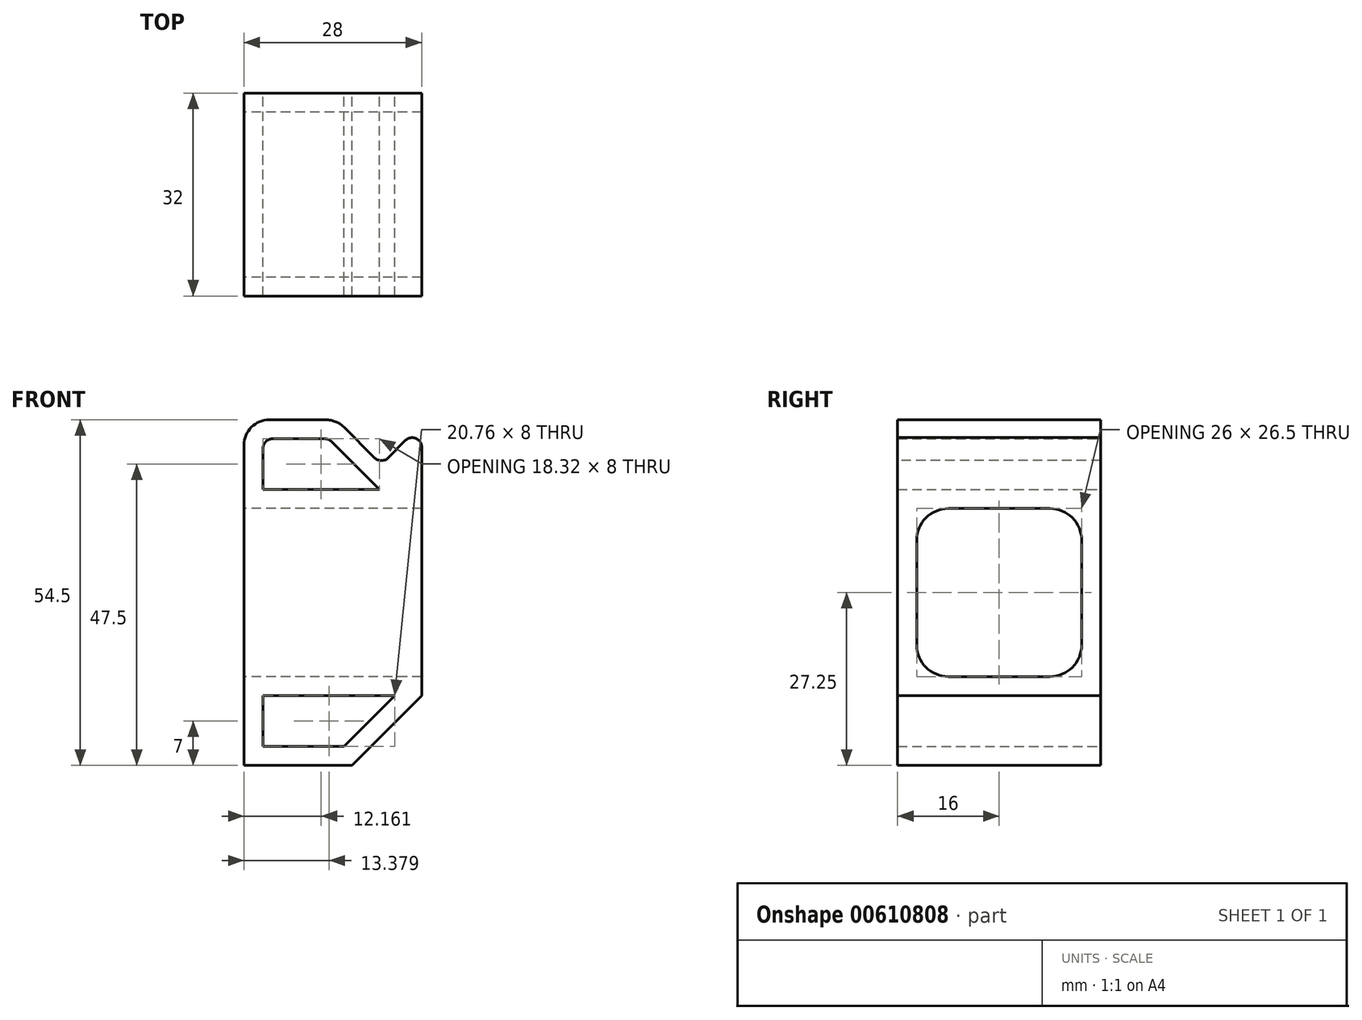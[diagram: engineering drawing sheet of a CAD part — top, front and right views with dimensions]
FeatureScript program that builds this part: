
annotation { "Feature Type Name" : "Feature", "Feature Type Description" : "" }
export const myFeature = defineFeature(function(context is Context, id is Id, definition is map)
    precondition{}
    {
        {
            var Q0;
            Q0=qCreatedBy(makeId("Right.planeOp"),FACE);
            var sketch = newSketch(context, id + "F0", { "sketchPlane" : qUnion([Q0])});
            skLineSegment(sketch, "E0.bottom", {"start": v(13, 13.25) * mm, "end": v(-13, 13.25) * mm});
            skLineSegment(sketch, "E0.top", {"start": v(13, -13.25) * mm, "end": v(-13, -13.25) * mm});
            skLineSegment(sketch, "E0.left", {"start": v(13, 13.25) * mm, "end": v(13, -13.25) * mm});
            skLineSegment(sketch, "E0.right", {"start": v(-13, 13.25) * mm, "end": v(-13, -13.25) * mm});
            skPoint(sketch, "E0.middle", {"position": v(0, 0) * mm});
            skLineSegment(sketch, "E1.bottom", {"start": v(16, 16.25) * mm, "end": v(-16, 16.25) * mm});
            skLineSegment(sketch, "E1.top", {"start": v(16, -16.25) * mm, "end": v(-16, -16.25) * mm});
            skLineSegment(sketch, "E1.left", {"start": v(16, 16.25) * mm, "end": v(16, -16.25) * mm});
            skLineSegment(sketch, "E1.right", {"start": v(-16, 16.25) * mm, "end": v(-16, -16.25) * mm});
            skSolve(sketch);
        }
        {
            var Q0;
            Q0 = qSketchRegion(id + "F0", true);
            extrude(context, id + "F1", {"entities" : qUnion([Q0]), "depth" : 28 * mm, "offsetDistance" : 25 * mm});
        }
        {
            var Q0;
            Q0=qCreatedBy(makeId("Front.planeOp"),FACE);
            var sketch = newSketch(context, id + "F2", { "sketchPlane" : qUnion([Q0])});
            skLineSegment(sketch, "E2", {"start": v(28, 16.25) * mm, "end": v(28, 26.54) * mm});
            skLineSegment(sketch, "E3", {"start": v(28, 26.54) * mm, "end": v(21.64, 20.18) * mm});
            skLineSegment(sketch, "E4", {"start": v(21.64, 20.18) * mm, "end": v(14.56, 27.25) * mm});
            skLineSegment(sketch, "E5", {"start": v(14.56, 27.25) * mm, "end": v(0, 27.25) * mm});
            skLineSegment(sketch, "E6", {"start": v(0, 27.25) * mm, "end": v(0, 16.25) * mm});
            skLineSegment(sketch, "E7.0", {"start": v(21.32, 16.25) * mm, "end": v(3, 16.25) * mm});
            skLineSegment(sketch, "E7.1", {"start": v(3, 24.25) * mm, "end": v(3, 16.25) * mm});
            skLineSegment(sketch, "E7.2", {"start": v(13.32, 24.25) * mm, "end": v(3, 24.25) * mm});
            skLineSegment(sketch, "E7.3", {"start": v(21.32, 16.25) * mm, "end": v(13.32, 24.25) * mm});
            skLineSegment(sketch, "E8", {"start": v(0, 16.25) * mm, "end": v(28, 16.25) * mm});
            skLineSegment(sketch, "E9.2", {"start": v(45.18, 16.25) * mm, "end": v(-18.36, 16.25) * mm, "construction": true});
            skSolve(sketch);
        }
        {
            var Q0;
            {var subQ0=sQuery(id+"F2.wireOp",EDGE,"E2");Q0=makeQuery(id+"F2.imprint","IMPRINT",FACE,{"disambiguationData":[TD([[makeQuery(id+"F2.imprint","IMPRINT",EDGE,{"derivedFrom":subQ0}),1.0]])]});}
            var Q1;
            Q1=makeQuery(id+"F1.opExtrude","SWEPT_FACE",FACE,{"disambiguationData":[OSD([sQuery(id+"F0.wireOp",EDGE,"E1.right")])]});
            var Q2;
            Q2=makeQuery(id+"F1.opExtrude","SWEPT_FACE",FACE,{"disambiguationData":[OSD([sQuery(id+"F0.wireOp",EDGE,"ShcMqtXd-iH10-RJuc-bSqI-YvODFhP9SOUm")])]});
            extrude(context, id + "F3", {"entities" : qUnion([Q0]), "operationType" : NewBodyOperationType.ADD, "endBound" : BoundingType.SYMMETRIC, "depth" : 32 * mm, "endBoundEntityFace" : qUnion([Q1]), "offsetDistance" : 25 * mm, "hasSecondDirection" : true, "secondDirectionBound" : SecondDirectionBoundingType.UP_TO_SURFACE, "secondDirectionOppositeDirection" : true, "secondDirectionDepth" : 25 * mm, "secondDirectionBoundEntityFace" : qUnion([Q2])});
        }
        {
            var Q0;
            Q0=qCreatedBy(makeId("Front.planeOp"),FACE);
            var sketch = newSketch(context, id + "F4", { "sketchPlane" : qUnion([Q0])});
            skLineSegment(sketch, "E10.0.1", {"start": v(0, -16.25) * mm, "end": v(28, -16.25) * mm});
            skLineSegment(sketch, "E11.bottom", {"start": v(0, -27.25) * mm, "end": v(17, -27.25) * mm});
            skLineSegment(sketch, "E11.right", {"start": v(0, -16.25) * mm, "end": v(0, -27.25) * mm});
            skLineSegment(sketch, "E12", {"start": v(28, -16.25) * mm, "end": v(17, -27.25) * mm});
            skLineSegment(sketch, "E13.0", {"start": v(23.76, -16.25) * mm, "end": v(15.76, -24.25) * mm});
            skLineSegment(sketch, "E13.1", {"start": v(3, -24.25) * mm, "end": v(15.76, -24.25) * mm});
            skLineSegment(sketch, "E13.2", {"start": v(3, -16.25) * mm, "end": v(3, -24.25) * mm});
            skSolve(sketch);
        }
        {
            var Q0;
            Q0=makeQuery(id+"F4.imprint","IMPRINT",FACE,{"disambiguationData":[TD([[makeQuery(id+"F4.imprint","IMPRINT",EDGE,{"derivedFrom":sQuery(id+"F4.wireOp",EDGE,"E11.bottom")}),1.0]])]});
            var Q1;
            Q1=makeQuery(id+"F1.opExtrude","CAP_VERTEX",VERTEX,{"disambiguationData":[OSD([sQuery(id+"F0.wireOp",EDGE,"E1.top"),sQuery(id+"F0.wireOp",EDGE,"E1.right"),sQuery(id+"F0.wireOp",EDGE,"f836a4ea-6556-4c57-9a7b-fc94dc2d46c80.MirrorCS")])],"isStart":false});
            var Q2;
            Q2=makeQuery(id+"F1.opExtrude","CAP_VERTEX",VERTEX,{"disambiguationData":[OSD([sQuery(id+"F0.wireOp",EDGE,"E1.top"),sQuery(id+"F0.wireOp",EDGE,"E1.left"),sQuery(id+"F0.wireOp",EDGE,"1c46fe3f-ea86-4cfc-81d0-2548a7b6d6ba")])],"isStart":false});
            extrude(context, id + "F5", {"entities" : qUnion([Q0]), "operationType" : NewBodyOperationType.ADD, "endBound" : BoundingType.UP_TO_VERTEX, "depth" : 25 * mm, "endBoundEntityVertex" : qUnion([Q1]), "offsetDistance" : 25 * mm, "hasSecondDirection" : true, "secondDirectionBound" : SecondDirectionBoundingType.UP_TO_VERTEX, "secondDirectionOppositeDirection" : true, "secondDirectionDepth" : 25 * mm, "secondDirectionBoundEntityVertex" : qUnion([Q2])});
        }
        {
            var Q0;
            Q0=makeQuery(id+"F1.opExtrude","SWEPT_EDGE",EDGE,{"disambiguationData":[OSD([sQuery(id+"F0.wireOp",EDGE,"E0.top"),sQuery(id+"F0.wireOp",EDGE,"E0.left")])]});
            var Q1;
            Q1=makeQuery(id+"F1.opExtrude","SWEPT_EDGE",EDGE,{"disambiguationData":[OSD([sQuery(id+"F0.wireOp",EDGE,"E0.bottom"),sQuery(id+"F0.wireOp",EDGE,"E0.left")])]});
            var Q2;
            Q2=makeQuery(id+"F1.opExtrude","SWEPT_EDGE",EDGE,{"disambiguationData":[OSD([sQuery(id+"F0.wireOp",EDGE,"E0.bottom"),sQuery(id+"F0.wireOp",EDGE,"E0.right")])]});
            var Q3;
            Q3=makeQuery(id+"F1.opExtrude","SWEPT_EDGE",EDGE,{"disambiguationData":[OSD([sQuery(id+"F0.wireOp",EDGE,"E0.top"),sQuery(id+"F0.wireOp",EDGE,"E0.right")])]});
            fillet(context, id + "F6", {"entities" : qUnion([Q0, Q1, Q2, Q3]), "radius" : 5 * mm, "tangentPropagation" : true, "allowEdgeOverflow" : false});
        }
        {
            var Q0;
            {var subQ0=sQuery(id+"F2.wireOp",EDGE,"E8");var subQ1=sQuery(id+"F2.wireOp",EDGE,"E7.1");Q0=makeQuery(id+"F3.opExtrude","TWEAK_EDGE",EDGE,{"derivedFrom":[makeQuery(id+"F2.imprint","IMPRINT",EDGE,{"derivedFrom":subQ1}),makeQuery(id+"F2.imprint","IMPRINT",EDGE,{"disambiguationData":[TD([[makeQuery(id+"F2.imprint","INTERSECT",VERTEX,{"derivedFrom":[sQuery(id+"F2.wireOp",EDGE,"E6"),subQ0]}),-1.0]])],"derivedFrom":subQ0})]});}
            var Q1;
            Q1=makeQuery(id+"F3.opExtrude","TWEAK_EDGE",EDGE,{"derivedFrom":[makeQuery(id+"F2.imprint","IMPRINT",EDGE,{"derivedFrom":sQuery(id+"F2.wireOp",EDGE,"E7.1")}),makeQuery(id+"F2.imprint","IMPRINT",EDGE,{"derivedFrom":sQuery(id+"F2.wireOp",EDGE,"E7.2")})]});
            var Q2;
            Q2=makeQuery(id+"F3.opExtrude","TWEAK_EDGE",EDGE,{"derivedFrom":[makeQuery(id+"F2.imprint","IMPRINT",EDGE,{"derivedFrom":sQuery(id+"F2.wireOp",EDGE,"E7.2")}),makeQuery(id+"F2.imprint","IMPRINT",EDGE,{"derivedFrom":sQuery(id+"F2.wireOp",EDGE,"E7.3")})]});
            var Q3;
            {var subQ0=sQuery(id+"F2.wireOp",EDGE,"E8");var subQ1=sQuery(id+"F2.wireOp",EDGE,"E7.3");Q3=makeQuery(id+"F3.opExtrude","TWEAK_EDGE",EDGE,{"derivedFrom":[makeQuery(id+"F2.imprint","IMPRINT",EDGE,{"derivedFrom":subQ1}),makeQuery(id+"F2.imprint","IMPRINT",EDGE,{"disambiguationData":[TD([[makeQuery(id+"F2.imprint","INTERSECT",VERTEX,{"derivedFrom":[sQuery(id+"F2.wireOp",EDGE,"E2"),subQ0]}),1.0]])],"derivedFrom":subQ0})]});}
            var Q4;
            Q4=makeQuery(id+"F3.opExtrude","TWEAK_EDGE",EDGE,{"derivedFrom":[makeQuery(id+"F2.imprint","IMPRINT",EDGE,{"derivedFrom":sQuery(id+"F2.wireOp",EDGE,"E3")}),makeQuery(id+"F2.imprint","IMPRINT",EDGE,{"derivedFrom":sQuery(id+"F2.wireOp",EDGE,"E4")})]});
            var Q5;
            Q5=makeQuery(id+"F3.opExtrude","TWEAK_EDGE",EDGE,{"derivedFrom":[makeQuery(id+"F2.imprint","IMPRINT",EDGE,{"derivedFrom":sQuery(id+"F2.wireOp",EDGE,"E2")}),makeQuery(id+"F2.imprint","IMPRINT",EDGE,{"derivedFrom":sQuery(id+"F2.wireOp",EDGE,"E3")})]});
            var Q6;
            {var subQ0=sQuery(id+"F4.wireOp",EDGE,"6675c8d8-0c5b-4f71-856a-6b2601ab7805.0");var subQ1=sQuery(id+"F4.wireOp",EDGE,"E10.0.1");Q6=makeQuery(id+"F5.opExtrude","TWEAK_EDGE",EDGE,{"derivedFrom":[makeQuery(id+"F4.imprint","IMPRINT",EDGE,{"disambiguationData":[TD([[makeQuery(id+"F4.imprint","INTERSECT",VERTEX,{"derivedFrom":[subQ1,sQuery(id+"F4.wireOp",EDGE,"E11.right")]}),-1.0]])],"derivedFrom":subQ1}),makeQuery(id+"F4.imprint","IMPRINT",EDGE,{"derivedFrom":subQ0})]});}
            var Q7;
            Q7=makeQuery(id+"F5.opExtrude","TWEAK_EDGE",EDGE,{"derivedFrom":[makeQuery(id+"F4.imprint","IMPRINT",EDGE,{"derivedFrom":sQuery(id+"F4.wireOp",EDGE,"6675c8d8-0c5b-4f71-856a-6b2601ab7805.0")}),makeQuery(id+"F4.imprint","IMPRINT",EDGE,{"derivedFrom":sQuery(id+"F4.wireOp",EDGE,"6675c8d8-0c5b-4f71-856a-6b2601ab7805.1")})]});
            var Q8;
            Q8=makeQuery(id+"F5.opExtrude","TWEAK_EDGE",EDGE,{"derivedFrom":[makeQuery(id+"F4.imprint","IMPRINT",EDGE,{"derivedFrom":sQuery(id+"F4.wireOp",EDGE,"6675c8d8-0c5b-4f71-856a-6b2601ab7805.1")}),makeQuery(id+"F4.imprint","IMPRINT",EDGE,{"derivedFrom":sQuery(id+"F4.wireOp",EDGE,"6675c8d8-0c5b-4f71-856a-6b2601ab7805.2")})]});
            var Q9;
            {var subQ0=sQuery(id+"F4.wireOp",EDGE,"6675c8d8-0c5b-4f71-856a-6b2601ab7805.2");var subQ1=sQuery(id+"F4.wireOp",EDGE,"E10.0.1");Q9=makeQuery(id+"F5.opExtrude","TWEAK_EDGE",EDGE,{"derivedFrom":[makeQuery(id+"F4.imprint","IMPRINT",EDGE,{"disambiguationData":[TD([[makeQuery(id+"F4.imprint","INTERSECT",VERTEX,{"derivedFrom":[subQ1,sQuery(id+"F4.wireOp",EDGE,"E11.left")]}),1.0]])],"derivedFrom":subQ1}),makeQuery(id+"F4.imprint","IMPRINT",EDGE,{"derivedFrom":subQ0})]});}
            var Q10;
            Q10=makeQuery(id+"F1.opExtrude","SWEPT_EDGE",EDGE,{"disambiguationData":[OSD([sQuery(id+"F0.wireOp",EDGE,"744365c5-ccf3-407b-9dc3-74a4dc237ff60.MirrorCS"),sQuery(id+"F0.wireOp",EDGE,"f836a4ea-6556-4c57-9a7b-fc94dc2d46c80.MirrorCS")])]});
            var Q11;
            Q11=makeQuery(id+"F1.opExtrude","SWEPT_EDGE",EDGE,{"disambiguationData":[OSD([sQuery(id+"F0.wireOp",EDGE,"ShcMqtXd-iH10-RJuc-bSqI-YvODFhP9SOUm"),sQuery(id+"F0.wireOp",EDGE,"1c46fe3f-ea86-4cfc-81d0-2548a7b6d6ba")])]});
            var Q12;
            {var subQ0=sQuery(id+"F4.wireOp",EDGE,"E13.2");var subQ1=sQuery(id+"F4.wireOp",EDGE,"E10.0.1");Q12=makeQuery(id+"F5.opExtrude","TWEAK_EDGE",EDGE,{"derivedFrom":[makeQuery(id+"F4.imprint","IMPRINT",EDGE,{"disambiguationData":[TD([[makeQuery(id+"F4.imprint","INTERSECT",VERTEX,{"derivedFrom":[subQ1,sQuery(id+"F4.wireOp",EDGE,"E11.right")]}),-1.0]])],"derivedFrom":subQ1}),makeQuery(id+"F4.imprint","IMPRINT",EDGE,{"derivedFrom":subQ0})]});}
            var Q13;
            {var subQ0=sQuery(id+"F4.wireOp",EDGE,"E13.0");var subQ1=sQuery(id+"F4.wireOp",EDGE,"E10.0.1");Q13=makeQuery(id+"F5.opExtrude","TWEAK_EDGE",EDGE,{"derivedFrom":[makeQuery(id+"F4.imprint","IMPRINT",EDGE,{"disambiguationData":[TD([[makeQuery(id+"F4.imprint","INTERSECT",VERTEX,{"derivedFrom":[subQ1,sQuery(id+"F4.wireOp",EDGE,"E12")]}),1.0]])],"derivedFrom":subQ1}),makeQuery(id+"F4.imprint","IMPRINT",EDGE,{"derivedFrom":subQ0})]});}
            var Q14;
            Q14=makeQuery(id+"F5.opExtrude","TWEAK_EDGE",EDGE,{"derivedFrom":[makeQuery(id+"F4.imprint","IMPRINT",EDGE,{"derivedFrom":sQuery(id+"F4.wireOp",EDGE,"E13.0")}),makeQuery(id+"F4.imprint","IMPRINT",EDGE,{"derivedFrom":sQuery(id+"F4.wireOp",EDGE,"E13.1")})]});
            var Q15;
            Q15=makeQuery(id+"F5.opExtrude","TWEAK_EDGE",EDGE,{"derivedFrom":[makeQuery(id+"F4.imprint","IMPRINT",EDGE,{"derivedFrom":sQuery(id+"F4.wireOp",EDGE,"E13.1")}),makeQuery(id+"F4.imprint","IMPRINT",EDGE,{"derivedFrom":sQuery(id+"F4.wireOp",EDGE,"E13.2")})]});
            var Q16;
            Q16=makeQuery(id+"F3.opExtrude","SWEPT_EDGE",EDGE,{"disambiguationData":[OSD([sQuery(id+"F2.wireOp",EDGE,"E7.1"),sQuery(id+"F2.wireOp",EDGE,"E8")])]});
            var Q17;
            Q17=makeQuery(id+"F3.opExtrude","SWEPT_EDGE",EDGE,{"disambiguationData":[OSD([sQuery(id+"F2.wireOp",EDGE,"E7.1"),sQuery(id+"F2.wireOp",EDGE,"E7.2")])]});
            var Q18;
            Q18=makeQuery(id+"F3.opExtrude","SWEPT_EDGE",EDGE,{"disambiguationData":[OSD([sQuery(id+"F2.wireOp",EDGE,"E7.2"),sQuery(id+"F2.wireOp",EDGE,"E7.3")])]});
            var Q19;
            Q19=makeQuery(id+"F3.opExtrude","SWEPT_EDGE",EDGE,{"disambiguationData":[OSD([sQuery(id+"F2.wireOp",EDGE,"E7.3"),sQuery(id+"F2.wireOp",EDGE,"E8")])]});
            var Q20;
            Q20=makeQuery(id+"F3.opExtrude","SWEPT_EDGE",EDGE,{"disambiguationData":[OSD([sQuery(id+"F2.wireOp",EDGE,"E2"),sQuery(id+"F2.wireOp",EDGE,"E3")])]});
            var Q21;
            Q21=makeQuery(id+"F3.opExtrude","SWEPT_EDGE",EDGE,{"disambiguationData":[OSD([sQuery(id+"F2.wireOp",EDGE,"E3"),sQuery(id+"F2.wireOp",EDGE,"E4")])]});
            fillet(context, id + "F7", {"entities" : qUnion([Q0, Q1, Q2, Q3, Q4, Q5, Q6, Q7, Q8, Q9, Q10, Q11, Q12, Q13, Q14, Q15, Q16, Q17, Q18, Q19, Q20, Q21]), "radius" : 1.5 * mm, "tangentPropagation" : true, "allowEdgeOverflow" : false});
        }
        {
            var Q0;
            Q0=makeQuery(id+"F3.opExtrude","TWEAK_EDGE",EDGE,{"derivedFrom":[makeQuery(id+"F2.imprint","IMPRINT",EDGE,{"derivedFrom":sQuery(id+"F2.wireOp",EDGE,"E5")}),makeQuery(id+"F2.imprint","IMPRINT",EDGE,{"derivedFrom":sQuery(id+"F2.wireOp",EDGE,"E6")})]});
            var Q1;
            Q1=makeQuery(id+"F3.opExtrude","TWEAK_EDGE",EDGE,{"derivedFrom":[makeQuery(id+"F2.imprint","IMPRINT",EDGE,{"derivedFrom":sQuery(id+"F2.wireOp",EDGE,"E4")}),makeQuery(id+"F2.imprint","IMPRINT",EDGE,{"derivedFrom":sQuery(id+"F2.wireOp",EDGE,"E5")})]});
            var Q2;
            Q2=makeQuery(id+"F5.opExtrude","TWEAK_EDGE",EDGE,{"derivedFrom":[makeQuery(id+"F4.imprint","IMPRINT",EDGE,{"derivedFrom":sQuery(id+"F4.wireOp",EDGE,"E11.bottom")}),makeQuery(id+"F4.imprint","IMPRINT",EDGE,{"derivedFrom":sQuery(id+"F4.wireOp",EDGE,"E11.right")})]});
            var Q3;
            Q3=makeQuery(id+"F5.opExtrude","TWEAK_EDGE",EDGE,{"derivedFrom":[makeQuery(id+"F4.imprint","IMPRINT",EDGE,{"derivedFrom":sQuery(id+"F4.wireOp",EDGE,"E11.bottom")}),makeQuery(id+"F4.imprint","IMPRINT",EDGE,{"derivedFrom":sQuery(id+"F4.wireOp",EDGE,"E11.left")})]});
            var Q4;
            Q4=makeQuery(id+"F5.opExtrude","TWEAK_EDGE",EDGE,{"derivedFrom":[makeQuery(id+"F4.imprint","IMPRINT",EDGE,{"derivedFrom":sQuery(id+"F4.wireOp",EDGE,"E11.bottom")}),makeQuery(id+"F4.imprint","IMPRINT",EDGE,{"derivedFrom":sQuery(id+"F4.wireOp",EDGE,"E12")})]});
            var Q5;
            Q5=makeQuery(id+"F3.opExtrude","SWEPT_EDGE",EDGE,{"disambiguationData":[OSD([sQuery(id+"F2.wireOp",EDGE,"E5"),sQuery(id+"F2.wireOp",EDGE,"E6")])]});
            var Q6;
            Q6=makeQuery(id+"F3.opExtrude","SWEPT_EDGE",EDGE,{"disambiguationData":[OSD([sQuery(id+"F2.wireOp",EDGE,"E4"),sQuery(id+"F2.wireOp",EDGE,"E5")])]});
            fillet(context, id + "F8", {"entities" : qUnion([Q0, Q1, Q2, Q3, Q4, Q5, Q6]), "radius" : 4 * mm, "tangentPropagation" : true, "allowEdgeOverflow" : false});
        }
    });
